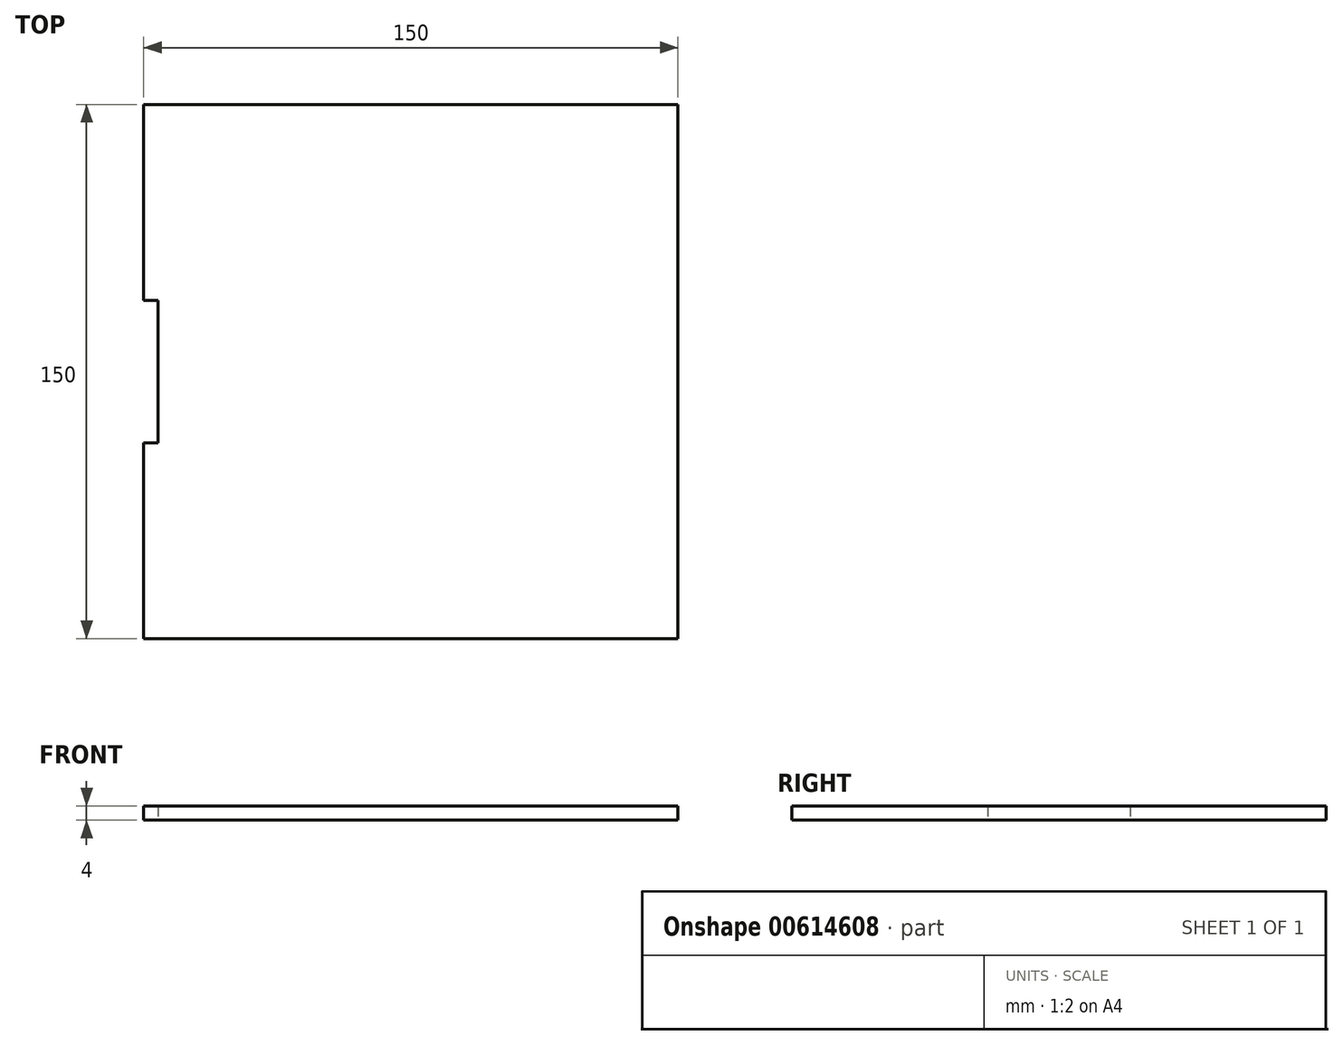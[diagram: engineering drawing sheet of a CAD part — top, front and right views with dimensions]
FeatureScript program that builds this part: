
annotation { "Feature Type Name" : "Feature", "Feature Type Description" : "" }
export const myFeature = defineFeature(function(context is Context, id is Id, definition is map)
    precondition{}
    {
        {
            var Q0;
            Q0=qCreatedBy(makeId("Top.planeOp"),FACE);
            var sketch = newSketch(context, id + "F0", { "sketchPlane" : qUnion([Q0])});
            skLineSegment(sketch, "E0.bottom", {"start": v(0, 0) * mm, "end": v(150, 0) * mm});
            skLineSegment(sketch, "E0.top", {"start": v(0, 150) * mm, "end": v(150, 150) * mm});
            skLineSegment(sketch, "E0.left", {"start": v(0, 0) * mm, "end": v(0, 150) * mm});
            skLineSegment(sketch, "E0.right", {"start": v(150, 0) * mm, "end": v(150, 150) * mm});
            skLineSegment(sketch, "E1", {"start": v(75, 150) * mm, "end": v(75, -24.94) * mm, "construction": true});
            skLineSegment(sketch, "E2", {"start": v(65, 150) * mm, "end": v(65, 130) * mm});
            skLineSegment(sketch, "E3", {"start": v(65, 128) * mm, "end": v(65, 109) * mm});
            skLineSegment(sketch, "E4", {"start": v(65, 107) * mm, "end": v(65, 87) * mm});
            skLineSegment(sketch, "E5", {"start": v(65, 87) * mm, "end": v(65, -49) * mm, "construction": true});
            skLineSegment(sketch, "E6", {"start": v(65, 85) * mm, "end": v(65, 65) * mm});
            skLineSegment(sketch, "E7", {"start": v(65, 63) * mm, "end": v(65, 43) * mm});
            skLineSegment(sketch, "E8", {"start": v(65, 41) * mm, "end": v(65, 21) * mm});
            skLineSegment(sketch, "E9", {"start": v(65, 0) * mm, "end": v(65, 19) * mm});
            skLineSegment(sketch, "E10", {"start": v(66, 119.5) * mm, "end": v(66, 139) * mm});
            skLineSegment(sketch, "E11", {"start": v(66, 141) * mm, "end": v(66, 150) * mm});
            skLineSegment(sketch, "E12", {"start": v(66, 117.5) * mm, "end": v(66, 98) * mm});
            skLineSegment(sketch, "E13", {"start": v(66, 96) * mm, "end": v(66, 76) * mm});
            skLineSegment(sketch, "E14", {"start": v(66, 74) * mm, "end": v(66, 54) * mm});
            skLineSegment(sketch, "E15", {"start": v(66, 52) * mm, "end": v(66, 32) * mm});
            skLineSegment(sketch, "E16", {"start": v(66, 30) * mm, "end": v(66, 10.5) * mm});
            skLineSegment(sketch, "E17", {"start": v(66, 8.5) * mm, "end": v(66, 0) * mm});
            skLineSegment(sketch, "E18", {"start": v(65, 118.5) * mm, "end": v(108.65, 118.5) * mm, "construction": true});
            skLineSegment(sketch, "E19", {"start": v(65, 140) * mm, "end": v(45.03, 140) * mm, "construction": true});
            skLineSegment(sketch, "E20", {"start": v(65, 97) * mm, "end": v(35.1, 97) * mm, "construction": true});
            skLineSegment(sketch, "E21", {"start": v(65, 75) * mm, "end": v(44.9, 75) * mm, "construction": true});
            skLineSegment(sketch, "E22", {"start": v(65, 53) * mm, "end": v(43.02, 53) * mm, "construction": true});
            skLineSegment(sketch, "E23", {"start": v(65, 31) * mm, "end": v(39.95, 31) * mm, "construction": true});
            skPoint(sketch, "E24.endSnap0", {"position": v(65, 9.5) * mm});
            skLineSegment(sketch, "E25", {"start": v(46.72, 9.5) * mm, "end": v(65, 9.5) * mm, "construction": true});
            skLineSegment(sketch, "E26.1.0.0", {"start": v(68, 117.5) * mm, "end": v(68, 98) * mm});
            skLineSegment(sketch, "E26.1.0.1", {"start": v(68, 74) * mm, "end": v(68, 54) * mm});
            skLineSegment(sketch, "E26.1.0.2", {"start": v(67, 107) * mm, "end": v(67, 87) * mm});
            skLineSegment(sketch, "E26.1.0.3", {"start": v(67, 63) * mm, "end": v(67, 43) * mm});
            skLineSegment(sketch, "E26.1.0.4", {"start": v(68, 141) * mm, "end": v(68, 150) * mm});
            skPoint(sketch, "E26.1.0.5", {"position": v(67, 9.5) * mm});
            skLineSegment(sketch, "E26.1.0.6", {"start": v(67, 41) * mm, "end": v(67, 21) * mm});
            skLineSegment(sketch, "E26.1.0.7", {"start": v(68, 119.5) * mm, "end": v(68, 139) * mm});
            skLineSegment(sketch, "E26.1.0.8", {"start": v(68, 30) * mm, "end": v(68, 10.5) * mm});
            skLineSegment(sketch, "E26.1.0.9", {"start": v(67, 85) * mm, "end": v(67, 65) * mm});
            skLineSegment(sketch, "E26.1.0.10", {"start": v(67, 150) * mm, "end": v(67, 130) * mm});
            skLineSegment(sketch, "E26.1.0.11", {"start": v(67, 0) * mm, "end": v(67, 19) * mm});
            skLineSegment(sketch, "E26.1.0.12", {"start": v(67, 128) * mm, "end": v(67, 109) * mm});
            skLineSegment(sketch, "E26.1.0.13", {"start": v(68, 96) * mm, "end": v(68, 76) * mm});
            skLineSegment(sketch, "E26.1.0.14", {"start": v(68, 8.5) * mm, "end": v(68, 0) * mm});
            skLineSegment(sketch, "E26.1.0.15", {"start": v(68, 52) * mm, "end": v(68, 32) * mm});
            skLineSegment(sketch, "E26.2.0.0", {"start": v(70, 117.5) * mm, "end": v(70, 98) * mm});
            skLineSegment(sketch, "E26.2.0.1", {"start": v(70, 74) * mm, "end": v(70, 54) * mm});
            skLineSegment(sketch, "E26.2.0.2", {"start": v(69, 107) * mm, "end": v(69, 87) * mm});
            skLineSegment(sketch, "E26.2.0.3", {"start": v(69, 63) * mm, "end": v(69, 43) * mm});
            skLineSegment(sketch, "E26.2.0.4", {"start": v(70, 141) * mm, "end": v(70, 150) * mm});
            skPoint(sketch, "E26.2.0.5", {"position": v(69, 9.5) * mm});
            skLineSegment(sketch, "E26.2.0.6", {"start": v(69, 41) * mm, "end": v(69, 21) * mm});
            skLineSegment(sketch, "E26.2.0.7", {"start": v(70, 119.5) * mm, "end": v(70, 139) * mm});
            skLineSegment(sketch, "E26.2.0.8", {"start": v(70, 30) * mm, "end": v(70, 10.5) * mm});
            skLineSegment(sketch, "E26.2.0.9", {"start": v(69, 85) * mm, "end": v(69, 65) * mm});
            skLineSegment(sketch, "E26.2.0.10", {"start": v(69, 150) * mm, "end": v(69, 130) * mm});
            skLineSegment(sketch, "E26.2.0.11", {"start": v(69, 0) * mm, "end": v(69, 19) * mm});
            skLineSegment(sketch, "E26.2.0.12", {"start": v(69, 128) * mm, "end": v(69, 109) * mm});
            skLineSegment(sketch, "E26.2.0.13", {"start": v(70, 96) * mm, "end": v(70, 76) * mm});
            skLineSegment(sketch, "E26.2.0.14", {"start": v(70, 8.5) * mm, "end": v(70, 0) * mm});
            skLineSegment(sketch, "E26.2.0.15", {"start": v(70, 52) * mm, "end": v(70, 32) * mm});
            skLineSegment(sketch, "E26.3.0.0", {"start": v(72, 117.5) * mm, "end": v(72, 98) * mm});
            skLineSegment(sketch, "E26.3.0.1", {"start": v(72, 74) * mm, "end": v(72, 54) * mm});
            skLineSegment(sketch, "E26.3.0.2", {"start": v(71, 107) * mm, "end": v(71, 87) * mm});
            skLineSegment(sketch, "E26.3.0.3", {"start": v(71, 63) * mm, "end": v(71, 43) * mm});
            skLineSegment(sketch, "E26.3.0.4", {"start": v(72, 141) * mm, "end": v(72, 150) * mm});
            skPoint(sketch, "E26.3.0.5", {"position": v(71, 9.5) * mm});
            skLineSegment(sketch, "E26.3.0.6", {"start": v(71, 41) * mm, "end": v(71, 21) * mm});
            skLineSegment(sketch, "E26.3.0.7", {"start": v(72, 119.5) * mm, "end": v(72, 139) * mm});
            skLineSegment(sketch, "E26.3.0.8", {"start": v(72, 30) * mm, "end": v(72, 10.5) * mm});
            skLineSegment(sketch, "E26.3.0.9", {"start": v(71, 85) * mm, "end": v(71, 65) * mm});
            skLineSegment(sketch, "E26.3.0.10", {"start": v(71, 150) * mm, "end": v(71, 130) * mm});
            skLineSegment(sketch, "E26.3.0.11", {"start": v(71, 0) * mm, "end": v(71, 19) * mm});
            skLineSegment(sketch, "E26.3.0.12", {"start": v(71, 128) * mm, "end": v(71, 109) * mm});
            skLineSegment(sketch, "E26.3.0.13", {"start": v(72, 96) * mm, "end": v(72, 76) * mm});
            skLineSegment(sketch, "E26.3.0.14", {"start": v(72, 8.5) * mm, "end": v(72, 0) * mm});
            skLineSegment(sketch, "E26.3.0.15", {"start": v(72, 52) * mm, "end": v(72, 32) * mm});
            skLineSegment(sketch, "E26.4.0.0", {"start": v(74, 117.5) * mm, "end": v(74, 98) * mm});
            skLineSegment(sketch, "E26.4.0.1", {"start": v(74, 74) * mm, "end": v(74, 54) * mm});
            skLineSegment(sketch, "E26.4.0.2", {"start": v(73, 107) * mm, "end": v(73, 87) * mm});
            skLineSegment(sketch, "E26.4.0.3", {"start": v(73, 63) * mm, "end": v(73, 43) * mm});
            skLineSegment(sketch, "E26.4.0.4", {"start": v(74, 141) * mm, "end": v(74, 150) * mm});
            skPoint(sketch, "E26.4.0.5", {"position": v(73, 9.5) * mm});
            skLineSegment(sketch, "E26.4.0.6", {"start": v(73, 41) * mm, "end": v(73, 21) * mm});
            skLineSegment(sketch, "E26.4.0.7", {"start": v(74, 119.5) * mm, "end": v(74, 139) * mm});
            skLineSegment(sketch, "E26.4.0.8", {"start": v(74, 30) * mm, "end": v(74, 10.5) * mm});
            skLineSegment(sketch, "E26.4.0.9", {"start": v(73, 85) * mm, "end": v(73, 65) * mm});
            skLineSegment(sketch, "E26.4.0.10", {"start": v(73, 150) * mm, "end": v(73, 130) * mm});
            skLineSegment(sketch, "E26.4.0.11", {"start": v(73, 0) * mm, "end": v(73, 19) * mm});
            skLineSegment(sketch, "E26.4.0.12", {"start": v(73, 128) * mm, "end": v(73, 109) * mm});
            skLineSegment(sketch, "E26.4.0.13", {"start": v(74, 96) * mm, "end": v(74, 76) * mm});
            skLineSegment(sketch, "E26.4.0.14", {"start": v(74, 8.5) * mm, "end": v(74, 0) * mm});
            skLineSegment(sketch, "E26.4.0.15", {"start": v(74, 52) * mm, "end": v(74, 32) * mm});
            skLineSegment(sketch, "E26.5.0.0", {"start": v(76, 117.5) * mm, "end": v(76, 98) * mm});
            skLineSegment(sketch, "E26.5.0.1", {"start": v(76, 74) * mm, "end": v(76, 54) * mm});
            skLineSegment(sketch, "E26.5.0.2", {"start": v(75, 107) * mm, "end": v(75, 87) * mm});
            skLineSegment(sketch, "E26.5.0.3", {"start": v(75, 63) * mm, "end": v(75, 43) * mm});
            skLineSegment(sketch, "E26.5.0.4", {"start": v(76, 141) * mm, "end": v(76, 150) * mm});
            skPoint(sketch, "E26.5.0.5", {"position": v(75, 9.5) * mm});
            skLineSegment(sketch, "E26.5.0.6", {"start": v(75, 41) * mm, "end": v(75, 21) * mm});
            skLineSegment(sketch, "E26.5.0.7", {"start": v(76, 119.5) * mm, "end": v(76, 139) * mm});
            skLineSegment(sketch, "E26.5.0.8", {"start": v(76, 30) * mm, "end": v(76, 10.5) * mm});
            skLineSegment(sketch, "E26.5.0.9", {"start": v(75, 85) * mm, "end": v(75, 65) * mm});
            skLineSegment(sketch, "E26.5.0.10", {"start": v(75, 150) * mm, "end": v(75, 130) * mm});
            skLineSegment(sketch, "E26.5.0.11", {"start": v(75, 0) * mm, "end": v(75, 19) * mm});
            skLineSegment(sketch, "E26.5.0.12", {"start": v(75, 128) * mm, "end": v(75, 109) * mm});
            skLineSegment(sketch, "E26.5.0.13", {"start": v(76, 96) * mm, "end": v(76, 76) * mm});
            skLineSegment(sketch, "E26.5.0.14", {"start": v(76, 8.5) * mm, "end": v(76, 0) * mm});
            skLineSegment(sketch, "E26.5.0.15", {"start": v(76, 52) * mm, "end": v(76, 32) * mm});
            skLineSegment(sketch, "E26.6.0.0", {"start": v(78, 117.5) * mm, "end": v(78, 98) * mm});
            skLineSegment(sketch, "E26.6.0.1", {"start": v(78, 74) * mm, "end": v(78, 54) * mm});
            skLineSegment(sketch, "E26.6.0.2", {"start": v(77, 107) * mm, "end": v(77, 87) * mm});
            skLineSegment(sketch, "E26.6.0.3", {"start": v(77, 63) * mm, "end": v(77, 43) * mm});
            skLineSegment(sketch, "E26.6.0.4", {"start": v(78, 141) * mm, "end": v(78, 150) * mm});
            skPoint(sketch, "E26.6.0.5", {"position": v(77, 9.5) * mm});
            skLineSegment(sketch, "E26.6.0.6", {"start": v(77, 41) * mm, "end": v(77, 21) * mm});
            skLineSegment(sketch, "E26.6.0.7", {"start": v(78, 119.5) * mm, "end": v(78, 139) * mm});
            skLineSegment(sketch, "E26.6.0.8", {"start": v(78, 30) * mm, "end": v(78, 10.5) * mm});
            skLineSegment(sketch, "E26.6.0.9", {"start": v(77, 85) * mm, "end": v(77, 65) * mm});
            skLineSegment(sketch, "E26.6.0.10", {"start": v(77, 150) * mm, "end": v(77, 130) * mm});
            skLineSegment(sketch, "E26.6.0.11", {"start": v(77, 0) * mm, "end": v(77, 19) * mm});
            skLineSegment(sketch, "E26.6.0.12", {"start": v(77, 128) * mm, "end": v(77, 109) * mm});
            skLineSegment(sketch, "E26.6.0.13", {"start": v(78, 96) * mm, "end": v(78, 76) * mm});
            skLineSegment(sketch, "E26.6.0.14", {"start": v(78, 8.5) * mm, "end": v(78, 0) * mm});
            skLineSegment(sketch, "E26.6.0.15", {"start": v(78, 52) * mm, "end": v(78, 32) * mm});
            skLineSegment(sketch, "E26.7.0.0", {"start": v(80, 117.5) * mm, "end": v(80, 98) * mm});
            skLineSegment(sketch, "E26.7.0.1", {"start": v(80, 74) * mm, "end": v(80, 54) * mm});
            skLineSegment(sketch, "E26.7.0.2", {"start": v(79, 107) * mm, "end": v(79, 87) * mm});
            skLineSegment(sketch, "E26.7.0.3", {"start": v(79, 63) * mm, "end": v(79, 43) * mm});
            skLineSegment(sketch, "E26.7.0.4", {"start": v(80, 141) * mm, "end": v(80, 150) * mm});
            skPoint(sketch, "E26.7.0.5", {"position": v(79, 9.5) * mm});
            skLineSegment(sketch, "E26.7.0.6", {"start": v(79, 41) * mm, "end": v(79, 21) * mm});
            skLineSegment(sketch, "E26.7.0.7", {"start": v(80, 119.5) * mm, "end": v(80, 139) * mm});
            skLineSegment(sketch, "E26.7.0.8", {"start": v(80, 30) * mm, "end": v(80, 10.5) * mm});
            skLineSegment(sketch, "E26.7.0.9", {"start": v(79, 85) * mm, "end": v(79, 65) * mm});
            skLineSegment(sketch, "E26.7.0.10", {"start": v(79, 150) * mm, "end": v(79, 130) * mm});
            skLineSegment(sketch, "E26.7.0.11", {"start": v(79, 0) * mm, "end": v(79, 19) * mm});
            skLineSegment(sketch, "E26.7.0.12", {"start": v(79, 128) * mm, "end": v(79, 109) * mm});
            skLineSegment(sketch, "E26.7.0.13", {"start": v(80, 96) * mm, "end": v(80, 76) * mm});
            skLineSegment(sketch, "E26.7.0.14", {"start": v(80, 8.5) * mm, "end": v(80, 0) * mm});
            skLineSegment(sketch, "E26.7.0.15", {"start": v(80, 52) * mm, "end": v(80, 32) * mm});
            skLineSegment(sketch, "E26.8.0.0", {"start": v(82, 117.5) * mm, "end": v(82, 98) * mm});
            skLineSegment(sketch, "E26.8.0.1", {"start": v(82, 74) * mm, "end": v(82, 54) * mm});
            skLineSegment(sketch, "E26.8.0.2", {"start": v(81, 107) * mm, "end": v(81, 87) * mm});
            skLineSegment(sketch, "E26.8.0.3", {"start": v(81, 63) * mm, "end": v(81, 43) * mm});
            skLineSegment(sketch, "E26.8.0.4", {"start": v(82, 141) * mm, "end": v(82, 150) * mm});
            skPoint(sketch, "E26.8.0.5", {"position": v(81, 9.5) * mm});
            skLineSegment(sketch, "E26.8.0.6", {"start": v(81, 41) * mm, "end": v(81, 21) * mm});
            skLineSegment(sketch, "E26.8.0.7", {"start": v(82, 119.5) * mm, "end": v(82, 139) * mm});
            skLineSegment(sketch, "E26.8.0.8", {"start": v(82, 30) * mm, "end": v(82, 10.5) * mm});
            skLineSegment(sketch, "E26.8.0.9", {"start": v(81, 85) * mm, "end": v(81, 65) * mm});
            skLineSegment(sketch, "E26.8.0.10", {"start": v(81, 150) * mm, "end": v(81, 130) * mm});
            skLineSegment(sketch, "E26.8.0.11", {"start": v(81, 0) * mm, "end": v(81, 19) * mm});
            skLineSegment(sketch, "E26.8.0.12", {"start": v(81, 128) * mm, "end": v(81, 109) * mm});
            skLineSegment(sketch, "E26.8.0.13", {"start": v(82, 96) * mm, "end": v(82, 76) * mm});
            skLineSegment(sketch, "E26.8.0.14", {"start": v(82, 8.5) * mm, "end": v(82, 0) * mm});
            skLineSegment(sketch, "E26.8.0.15", {"start": v(82, 52) * mm, "end": v(82, 32) * mm});
            skLineSegment(sketch, "E26.9.0.0", {"start": v(84, 117.5) * mm, "end": v(84, 98) * mm});
            skLineSegment(sketch, "E26.9.0.1", {"start": v(84, 74) * mm, "end": v(84, 54) * mm});
            skLineSegment(sketch, "E26.9.0.2", {"start": v(83, 107) * mm, "end": v(83, 87) * mm});
            skLineSegment(sketch, "E26.9.0.3", {"start": v(83, 63) * mm, "end": v(83, 43) * mm});
            skLineSegment(sketch, "E26.9.0.4", {"start": v(84, 141) * mm, "end": v(84, 150) * mm});
            skPoint(sketch, "E26.9.0.5", {"position": v(83, 9.5) * mm});
            skLineSegment(sketch, "E26.9.0.6", {"start": v(83, 41) * mm, "end": v(83, 21) * mm});
            skLineSegment(sketch, "E26.9.0.7", {"start": v(84, 119.5) * mm, "end": v(84, 139) * mm});
            skLineSegment(sketch, "E26.9.0.8", {"start": v(84, 30) * mm, "end": v(84, 10.5) * mm});
            skLineSegment(sketch, "E26.9.0.9", {"start": v(83, 85) * mm, "end": v(83, 65) * mm});
            skLineSegment(sketch, "E26.9.0.10", {"start": v(83, 150) * mm, "end": v(83, 130) * mm});
            skLineSegment(sketch, "E26.9.0.11", {"start": v(83, 0) * mm, "end": v(83, 19) * mm});
            skLineSegment(sketch, "E26.9.0.12", {"start": v(83, 128) * mm, "end": v(83, 109) * mm});
            skLineSegment(sketch, "E26.9.0.13", {"start": v(84, 96) * mm, "end": v(84, 76) * mm});
            skLineSegment(sketch, "E26.9.0.14", {"start": v(84, 8.5) * mm, "end": v(84, 0) * mm});
            skLineSegment(sketch, "E26.9.0.15", {"start": v(84, 52) * mm, "end": v(84, 32) * mm});
            skLineSegment(sketch, "E26.direction1", {"start": v(65, 0) * mm, "end": v(67, 0) * mm, "construction": true});
            skSolve(sketch);
        }
        {
            var Q0;
            Q0=qCreatedBy(makeId("Top.planeOp"),FACE);
            var sketch = newSketch(context, id + "F1", { "sketchPlane" : qUnion([Q0])});
            skLineSegment(sketch, "E27.0", {"start": v(0, 0) * mm, "end": v(0, 150) * mm, "construction": true});
            skLineSegment(sketch, "E28.bottom", {"start": v(0, 95) * mm, "end": v(4, 95) * mm});
            skLineSegment(sketch, "E28.top", {"start": v(0, 55) * mm, "end": v(4, 55) * mm});
            skLineSegment(sketch, "E28.left", {"start": v(0, 95) * mm, "end": v(0, 55) * mm});
            skLineSegment(sketch, "E28.right", {"start": v(4, 95) * mm, "end": v(4, 55) * mm});
            skLineSegment(sketch, "E29", {"start": v(0, 75) * mm, "end": v(-100.46, 75) * mm, "construction": true});
            skSolve(sketch);
        }
        {
            var Q0;
            {var subQ0=sQuery(id+"F0.wireOp",EDGE,"E0.left");Q0=makeQuery(id+"F0.imprint","IMPRINT",FACE,{"disambiguationData":[TD([[makeQuery(id+"F0.imprint","IMPRINT",EDGE,{"derivedFrom":subQ0}),-1.0]])]});}
            extrude(context, id + "F2", {"entities" : qUnion([Q0]), "depth" : 4 * mm, "offsetDistance" : 25 * mm});
        }
        {
            var Q0;
            Q0 = qSketchRegion(id + "F1", true);
            var Q1;
            Q1=makeQuery(id+"F2.opExtrude","CAP_FACE",FACE,{"disambiguationData":[OSD([sQuery(id+"F0.wireOp",EDGE,"E0.bottom"),sQuery(id+"F0.wireOp",EDGE,"E0.top"),sQuery(id+"F0.wireOp",EDGE,"E0.left"),sQuery(id+"F0.wireOp",EDGE,"E0.right")])],"isStart":false});
            extrude(context, id + "F3", {"entities" : qUnion([Q0]), "operationType" : NewBodyOperationType.REMOVE, "endBound" : BoundingType.UP_TO_SURFACE, "depth" : 2 * mm, "endBoundEntityFace" : qUnion([Q1]), "offsetDistance" : 25 * mm});
        }
    });
